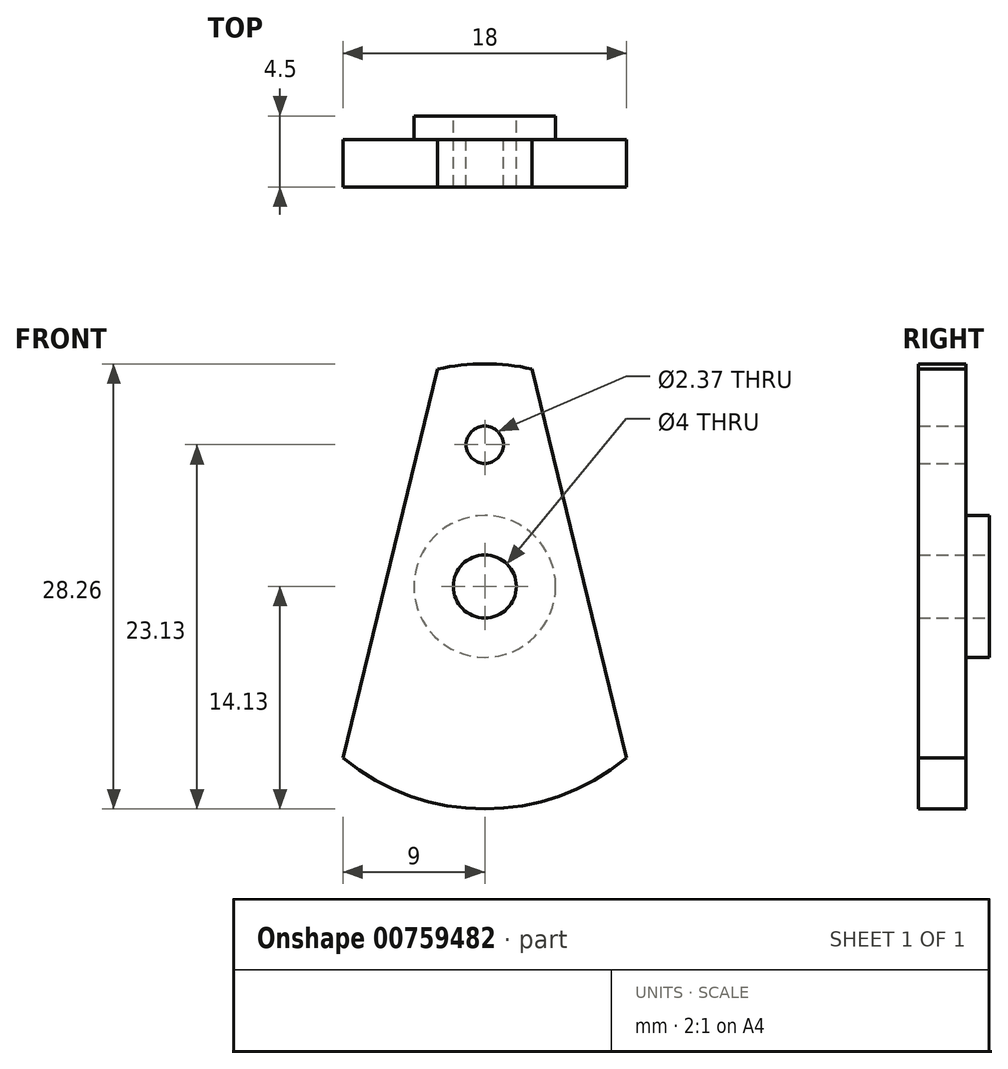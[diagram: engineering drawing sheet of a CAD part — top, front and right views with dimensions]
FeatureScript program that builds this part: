
annotation { "Feature Type Name" : "Feature", "Feature Type Description" : "" }
export const myFeature = defineFeature(function(context is Context, id is Id, definition is map)
    precondition{}
    {
        {
            var Q0;
            Q0=qCreatedBy(makeId("Front.planeOp"),FACE);
            var sketch = newSketch(context, id + "F0", { "sketchPlane" : qUnion([Q0])});
            skArc(sketch, "E0", {"start": v(3, 13.81) * mm, "mid": v(0, 14.13) * mm, "end": v(-3, 13.81) * mm});
            skCircle(sketch, "E1", {"center": v(0, 0) * mm, "radius": 4.5 * mm});
            skCircle(sketch, "E2", {"center": v(0, 0) * mm, "radius": 2 * mm});
            skLineSegment(sketch, "E3", {"start": v(3, 13.81) * mm, "end": v(9, -10.9) * mm});
            skLineSegment(sketch, "E4.MirrorCS", {"start": v(-3, 13.81) * mm, "end": v(-9, -10.9) * mm});
            skArc(sketch, "E5.trimOffspring", {"start": v(-9, -10.9) * mm, "mid": v(0, -14.13) * mm, "end": v(9, -10.9) * mm});
            skCircle(sketch, "E6", {"center": v(0, 9) * mm, "radius": 1.19 * mm});
            skSolve(sketch);
        }
        {
            var Q0;
            Q0 = qSketchRegion(id + "F0", true);
            var Q1;
            Q1=makeQuery(id+"F0.imprint","IMPRINT",FACE,{"disambiguationData":[TD([[makeQuery(id+"F0.imprint","IMPRINT",EDGE,{"derivedFrom":sQuery(id+"F0.wireOp",EDGE,"E1")}),1.0]])]});
            extrude(context, id + "F1", {"entities" : qUnion([Q0, Q1]), "depth" : 3 * mm, "offsetDistance" : 25 * mm});
        }
        {
            var Q0;
            Q0=makeQuery(id+"F0.imprint","IMPRINT",FACE,{"disambiguationData":[TD([[makeQuery(id+"F0.imprint","IMPRINT",EDGE,{"derivedFrom":sQuery(id+"F0.wireOp",EDGE,"E1")}),1.0]])]});
            extrude(context, id + "F2", {"entities" : qUnion([Q0]), "operationType" : NewBodyOperationType.ADD, "oppositeDirection" : true, "depth" : 1.5 * mm, "offsetDistance" : 25 * mm});
        }
    });
